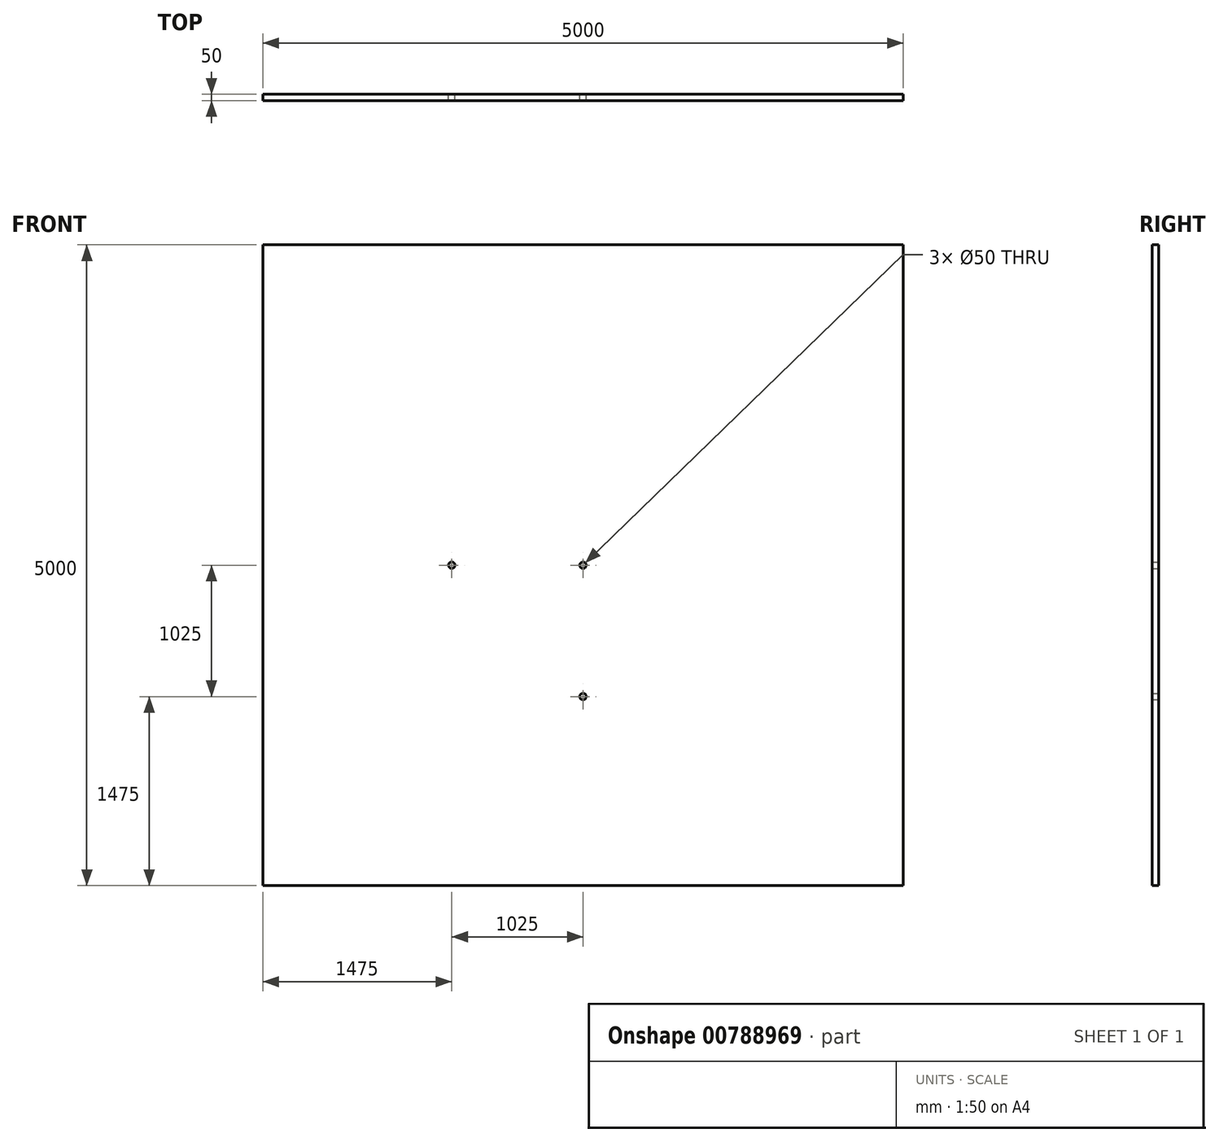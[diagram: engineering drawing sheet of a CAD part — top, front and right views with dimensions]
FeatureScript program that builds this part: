
annotation { "Feature Type Name" : "Feature", "Feature Type Description" : "" }
export const myFeature = defineFeature(function(context is Context, id is Id, definition is map)
    precondition{}
    {
        {
            var Q0;
            Q0=qCreatedBy(makeId("Front.planeOp"),FACE);
            var sketch = newSketch(context, id + "F0", { "sketchPlane" : qUnion([Q0])});
            skLineSegment(sketch, "E0.bottom", {"start": v(0, 0) * mm, "end": v(5000, 0) * mm});
            skLineSegment(sketch, "E0.top", {"start": v(0, 5000) * mm, "end": v(5000, 5000) * mm});
            skLineSegment(sketch, "E0.left", {"start": v(0, 0) * mm, "end": v(0, 5000) * mm});
            skLineSegment(sketch, "E0.right", {"start": v(5000, 0) * mm, "end": v(5000, 5000) * mm});
            skCircle(sketch, "E1", {"center": v(2500, 2500) * mm, "radius": 25 * mm});
            skPoint(sketch, "E1.centerSnap0", {"position": v(2500, 5000) * mm});
            skPoint(sketch, "E1.centerSnap1", {"position": v(0, 2500) * mm});
            skLineSegment(sketch, "E2", {"start": v(2475, 2500) * mm, "end": v(1475, 2500) * mm, "construction": true});
            skCircle(sketch, "E3", {"center": v(1475, 2500) * mm, "radius": 25 * mm});
            skLineSegment(sketch, "E4", {"start": v(2500, 2475) * mm, "end": v(2500, 1475) * mm, "construction": true});
            skCircle(sketch, "E5", {"center": v(2500, 1475) * mm, "radius": 25 * mm});
            skSolve(sketch);
        }
        {
            var Q0;
            Q0=makeQuery(id+"F0.imprint","IMPRINT",FACE,{"disambiguationData":[TD([[makeQuery(id+"F0.imprint","IMPRINT",EDGE,{"derivedFrom":sQuery(id+"F0.wireOp",EDGE,"E0.bottom")}),1.0]])]});
            extrude(context, id + "F1", {"entities" : qUnion([Q0]), "depth" : 50 * mm, "offsetDistance" : 25 * mm});
        }
    });
